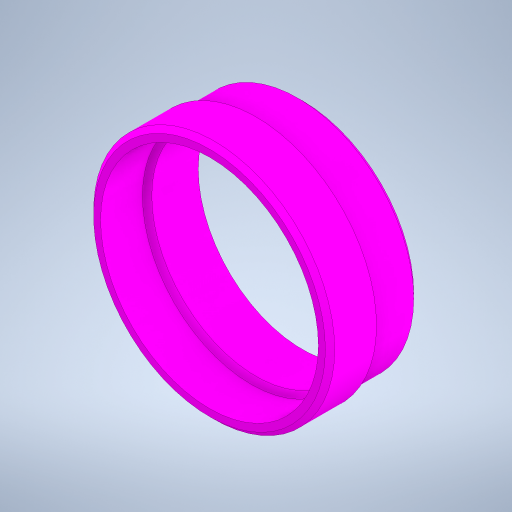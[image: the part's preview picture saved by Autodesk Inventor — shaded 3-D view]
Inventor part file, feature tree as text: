
AUTODESK INVENTOR PART (.ipt)
format: ipt  version: 2023.1 (Build 271208000, 208)  size: 260,096 bytes
history: native  units: mm
features: extrude x2, chamfer x2, sketch x1
ambient origin geometry x8: Origin, YZ Plane, XZ Plane, XY Plane, X Axis, Y Axis, Z Axis, Center Point
bodies: Solid1 (feature_tree)
feature tree (5):
  sketch  "Sketch1"  dims[d0=24.925mm d1=25.925mm d2=1.25mm d3=1.25mm d4=5.0mm d5=0.0mm d6=5.0mm d7=0.0mm d8=0.5mm d9=2.0mm d10=45.0deg d11=0.5mm d12=2.0mm d13=45.0deg]
  extrude  "Extrusion1"  Depth=5.0mm
  extrude  "Extrusion2"  Depth=5.0mm
  chamfer  "Chamfer1"  Distance=1.25mm
  chamfer  "Chamfer2"  Distance=5.0mm
